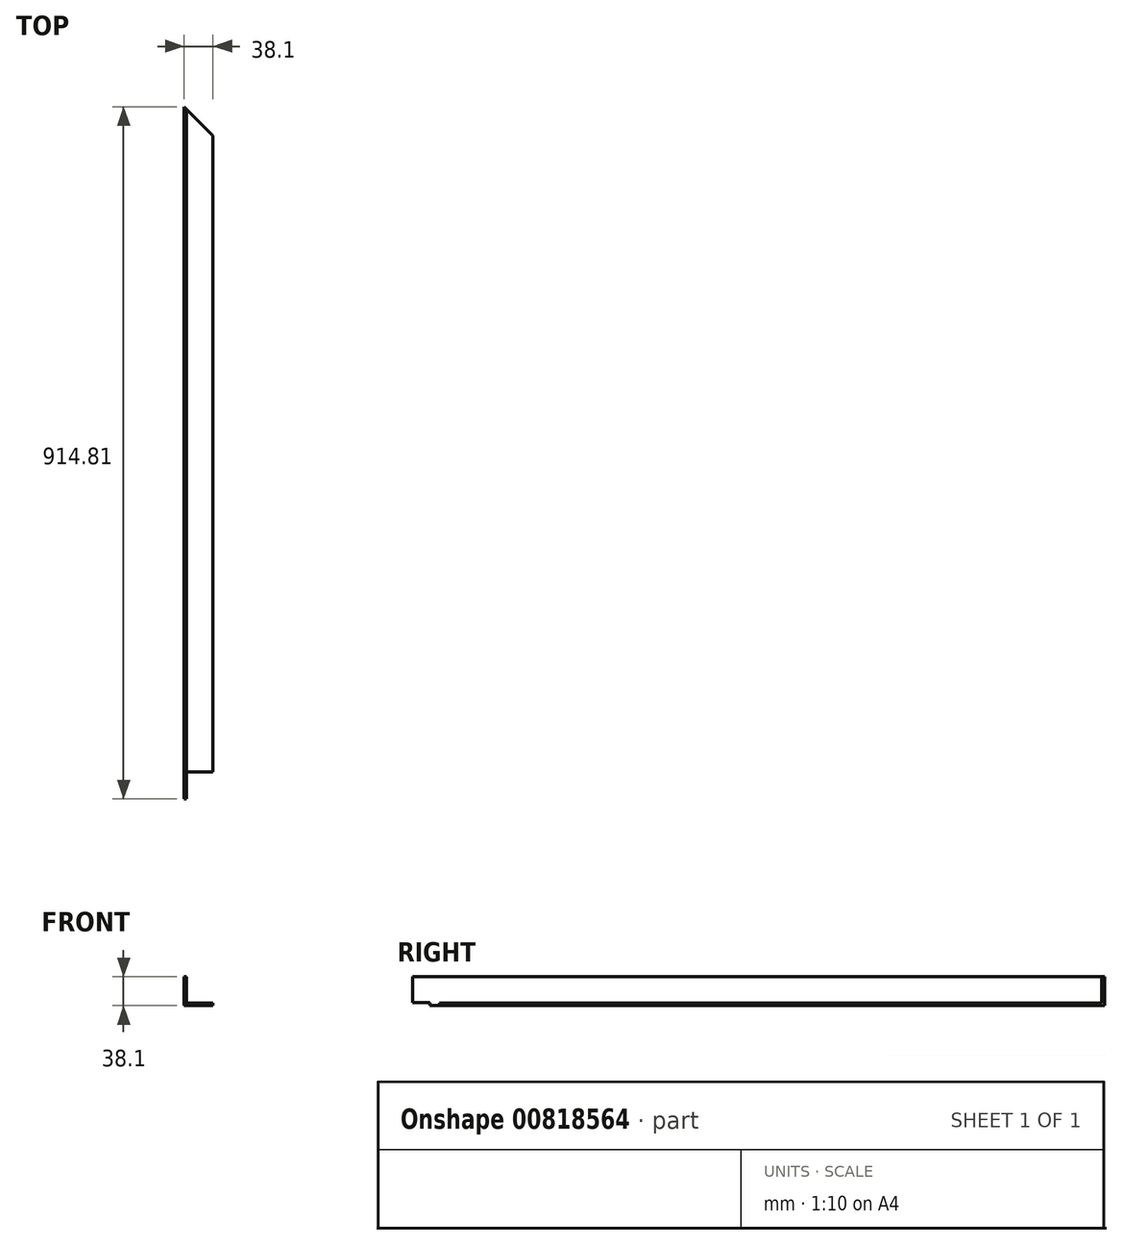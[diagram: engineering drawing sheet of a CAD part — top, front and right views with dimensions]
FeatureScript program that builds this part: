
annotation { "Feature Type Name" : "Feature", "Feature Type Description" : "" }
export const myFeature = defineFeature(function(context is Context, id is Id, definition is map)
    precondition{}
    {
        {
            var Q0;
            Q0=qCreatedBy(makeId("Front.planeOp"),FACE);
            var sketch = newSketch(context, id + "F0", { "sketchPlane" : qUnion([Q0])});
            skLineSegment(sketch, "E0", {"start": v(-21.73, 20.45) * mm, "end": v(-21.73, -17.65) * mm});
            skLineSegment(sketch, "E1", {"start": v(-21.73, -17.65) * mm, "end": v(16.37, -17.65) * mm});
            skLineSegment(sketch, "E2", {"start": v(16.37, -17.65) * mm, "end": v(16.37, -14.47) * mm});
            skLineSegment(sketch, "E3", {"start": v(16.37, -14.47) * mm, "end": v(-18.55, -14.47) * mm});
            skLineSegment(sketch, "E4", {"start": v(-18.55, -14.47) * mm, "end": v(-18.55, 20.45) * mm});
            skLineSegment(sketch, "E5", {"start": v(-18.55, 20.45) * mm, "end": v(-21.73, 20.45) * mm});
            skSolve(sketch);
        }
        {
            var Q0;
            Q0=makeQuery(id+"F0.imprint","IMPRINT",FACE,{"disambiguationData":[TD([[makeQuery(id+"F0.imprint","IMPRINT",EDGE,{"derivedFrom":sQuery(id+"F0.wireOp",EDGE,"E0")}),1.0]])]});
            extrude(context, id + "F1", {"entities" : qUnion([Q0]), "depth" : 914.8 * mm, "offsetDistance" : 25.4 * mm});
        }
        {
            var Q0;
            Q0=makeQuery(id+"F1.opExtrude","SWEPT_FACE",FACE,{"disambiguationData":[OSD([sQuery(id+"F0.wireOp",EDGE,"E3")])]});
            var sketch = newSketch(context, id + "F2", { "sketchPlane" : qUnion([Q0])});
            skLineSegment(sketch, "E6", {"start": v(-18.55, -914.8) * mm, "end": v(-18.55, -879.09) * mm});
            skLineSegment(sketch, "E7", {"start": v(-18.55, -879.09) * mm, "end": v(16.37, -879.09) * mm});
            skLineSegment(sketch, "E8", {"start": v(16.37, -879.09) * mm, "end": v(16.37, -914.8) * mm});
            skLineSegment(sketch, "E9", {"start": v(16.37, -914.8) * mm, "end": v(-18.55, -914.8) * mm});
            skSolve(sketch);
        }
        {
            var Q0;
            Q0=makeQuery(id+"F2.imprint","IMPRINT",FACE,{"disambiguationData":[TD([[makeQuery(id+"F2.imprint","IMPRINT",EDGE,{"derivedFrom":sQuery(id+"F2.wireOp",EDGE,"E6")}),-1.0]])]});
            extrude(context, id + "F3", {"entities" : qUnion([Q0]), "operationType" : NewBodyOperationType.REMOVE, "oppositeDirection" : true, "depth" : 25.4 * mm, "offsetDistance" : 25.4 * mm});
        }
        {
            var Q0;
            Q0=makeQuery(id+"F1.opExtrude","SWEPT_FACE",FACE,{"disambiguationData":[OSD([sQuery(id+"F0.wireOp",EDGE,"E1")])]});
            var sketch = newSketch(context, id + "F4", { "sketchPlane" : qUnion([Q0])});
            skLineSegment(sketch, "E10", {"start": v(-21.73, 0) * mm, "end": v(16.37, 38.1) * mm});
            skLineSegment(sketch, "E11", {"start": v(16.37, 38.1) * mm, "end": v(16.37, 0) * mm});
            skLineSegment(sketch, "E12", {"start": v(16.37, 0) * mm, "end": v(-21.73, 0) * mm});
            skSolve(sketch);
        }
        {
            var Q0;
            Q0 = qSketchRegion(id + "F4", true);
            extrude(context, id + "F5", {"entities" : qUnion([Q0]), "operationType" : NewBodyOperationType.REMOVE, "oppositeDirection" : true, "depth" : 38.1 * mm, "offsetDistance" : 25.4 * mm});
        }
        {
            var Q0;
            Q0=makeQuery(id+"F3.boolean.opBoolean","MERGE",FACE,{"derivedFrom":[makeQuery(id+"F1.opExtrude","SWEPT_FACE",FACE,{"disambiguationData":[OSD([sQuery(id+"F0.wireOp",EDGE,"E4")])]}),makeQuery(id+"F3.opExtrude","SWEPT_FACE",FACE,{"disambiguationData":[OSD([sQuery(id+"F2.wireOp",EDGE,"E6")])]})]});
            var sketch = newSketch(context, id + "F6", { "sketchPlane" : qUnion([Q0])});
            skLineSegment(sketch, "E13", {"start": v(-914.8, -17.65) * mm, "end": v(-914.8, -13.68) * mm});
            skLineSegment(sketch, "E14", {"start": v(-914.8, -13.68) * mm, "end": v(-891.79, -13.68) * mm});
            skLineSegment(sketch, "E15", {"start": v(-891.79, -13.68) * mm, "end": v(-891.79, -17.65) * mm});
            skLineSegment(sketch, "E16", {"start": v(-891.79, -17.65) * mm, "end": v(-914.8, -17.65) * mm});
            skSolve(sketch);
        }
        {
            var Q0;
            Q0=makeQuery(id+"F6.imprint","IMPRINT",FACE,{"disambiguationData":[TD([[makeQuery(id+"F6.imprint","IMPRINT",EDGE,{"derivedFrom":sQuery(id+"F6.wireOp",EDGE,"E13")}),-1.0]])]});
            extrude(context, id + "F7", {"entities" : qUnion([Q0]), "operationType" : NewBodyOperationType.REMOVE, "oppositeDirection" : true, "depth" : 25.4 * mm, "offsetDistance" : 25.4 * mm});
        }
        {
            var Q0;
            Q0=makeQuery(id+"F1.opExtrude","SWEPT_BODY",BODY,{"disambiguationData":[OSD([sQuery(id+"F0.wireOp",EDGE,"E0"),sQuery(id+"F0.wireOp",EDGE,"E1"),sQuery(id+"F0.wireOp",EDGE,"E2"),sQuery(id+"F0.wireOp",EDGE,"E3"),sQuery(id+"F0.wireOp",EDGE,"E4"),sQuery(id+"F0.wireOp",EDGE,"E5")])]});
            var Q1;
            Q1=makeQuery(id+"F1.opExtrude","SWEPT_FACE",FACE,{"disambiguationData":[OSD([sQuery(id+"F0.wireOp",EDGE,"E1")])]});
            mirror(context, id + "F8", {"operationType" : NewBodyOperationType.ADD, "entities" : qUnion([Q0]), "mirrorPlane" : qUnion([Q1])});
        }
        {
            var Q0;
            Q0=makeQuery(id+"F8.opPattern","COPY",FACE,{"derivedFrom":makeQuery(id+"F1.opExtrude","CAP_FACE",FACE,{"disambiguationData":[OSD([sQuery(id+"F0.wireOp",EDGE,"E0"),sQuery(id+"F0.wireOp",EDGE,"E1"),sQuery(id+"F0.wireOp",EDGE,"E2"),sQuery(id+"F0.wireOp",EDGE,"E3"),sQuery(id+"F0.wireOp",EDGE,"E4"),sQuery(id+"F0.wireOp",EDGE,"E5")])],"isStart":false}),"instanceName":"1"});
            var sketch = newSketch(context, id + "F9", { "sketchPlane" : qUnion([Q0])});
            skLineSegment(sketch, "E17", {"start": v(-21.73, -55.75) * mm, "end": v(-21.73, -17.65) * mm});
            skLineSegment(sketch, "E18", {"start": v(-21.73, -17.65) * mm, "end": v(16.37, -17.65) * mm});
            skLineSegment(sketch, "E19", {"start": v(16.37, -17.65) * mm, "end": v(16.37, -55.75) * mm});
            skLineSegment(sketch, "E20", {"start": v(16.37, -55.75) * mm, "end": v(-21.73, -55.75) * mm});
            skSolve(sketch);
        }
        {
            var Q0;
            Q0 = qSketchRegion(id + "F9", true);
            extrude(context, id + "F10", {"entities" : qUnion([Q0]), "operationType" : NewBodyOperationType.REMOVE, "endBound" : BoundingType.THROUGH_ALL, "oppositeDirection" : true, "depth" : 25.4 * mm, "offsetDistance" : 25.4 * mm});
        }
    });
